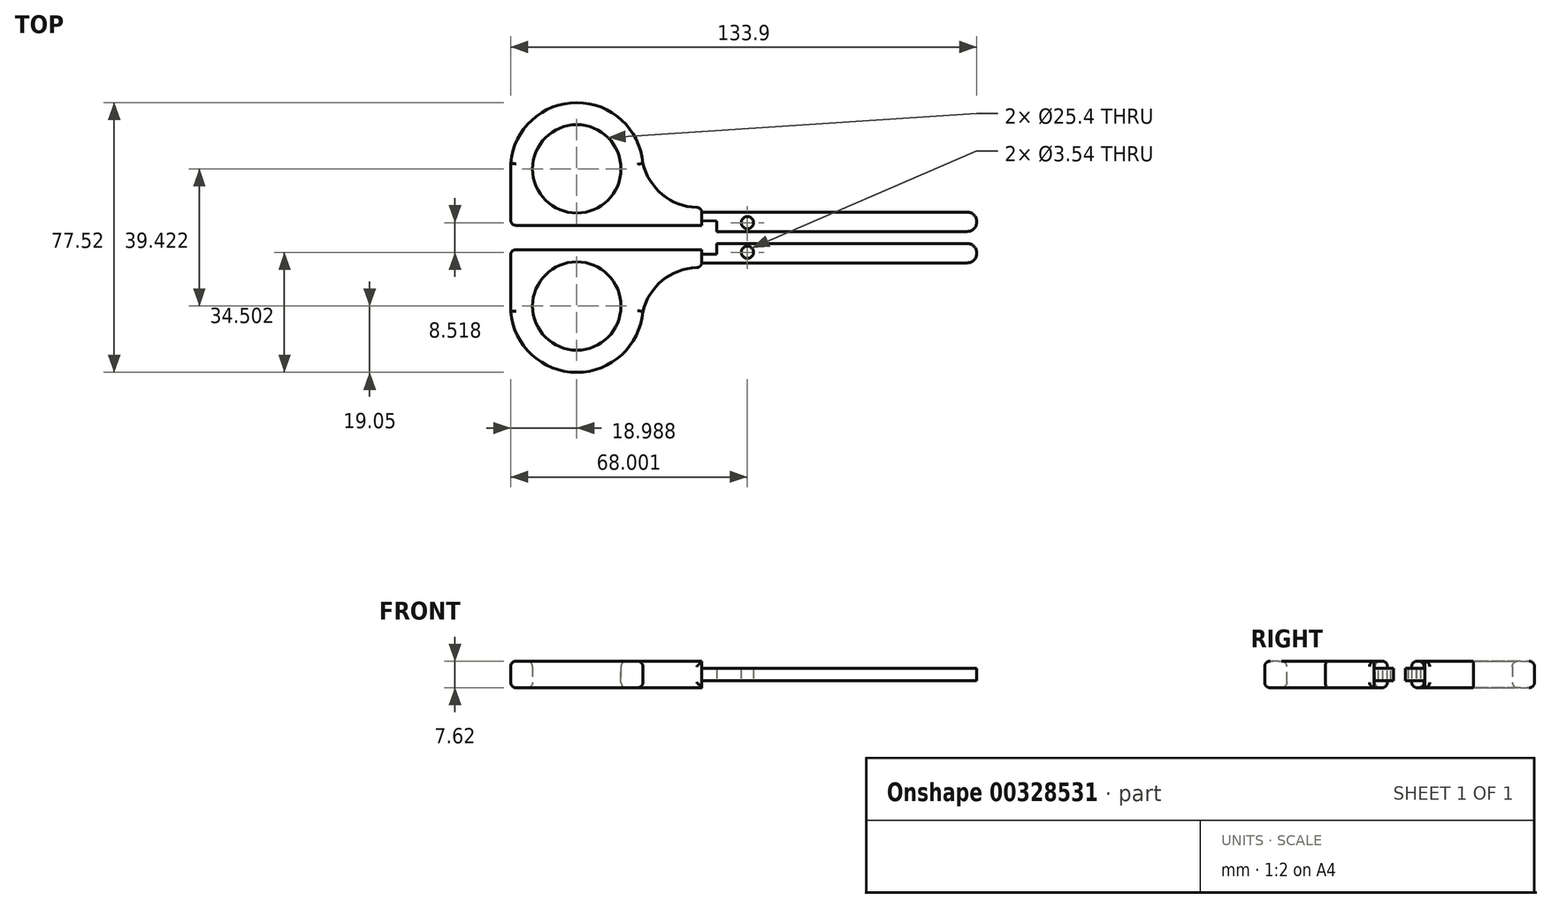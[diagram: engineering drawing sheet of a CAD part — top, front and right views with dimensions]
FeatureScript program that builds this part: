
annotation { "Feature Type Name" : "Feature", "Feature Type Description" : "" }
export const myFeature = defineFeature(function(context is Context, id is Id, definition is map)
    precondition{}
    {
        {
            var Q0;
            Q0=qCreatedBy(makeId("Top.planeOp"),FACE);
            var sketch = newSketch(context, id + "F0", { "sketchPlane" : qUnion([Q0])});
            skLineSegment(sketch, "E0", {"start": v(-55.55, 12.67) * mm, "end": v(-55.55, -5.11) * mm});
            skArc(sketch, "E1", {"start": v(-17.58, 12.67) * mm, "mid": v(-36.56, 30.16) * mm, "end": v(-55.55, 12.67) * mm});
            skLineSegment(sketch, "E2", {"start": v(-0.64, -1.3) * mm, "end": v(-0.64, -3.77) * mm});
            skLineSegment(sketch, "E3", {"start": v(-1.57, -5.11) * mm, "end": v(-55.55, -5.11) * mm});
            skCircle(sketch, "E4", {"center": v(-36.56, 11.11) * mm, "radius": 12.7 * mm});
            skLineSegment(sketch, "E5", {"start": v(-0.64, -1.3) * mm, "end": v(75.56, -1.3) * mm});
            skLineSegment(sketch, "E6", {"start": v(-0.64, -3.77) * mm, "end": v(3.68, -3.84) * mm});
            skCircle(sketch, "E7", {"center": v(12.45, -4.34) * mm, "radius": 1.77 * mm});
            skLineSegment(sketch, "E8", {"start": v(75.56, -6.88) * mm, "end": v(3.68, -6.88) * mm});
            skArc(sketch, "E9", {"start": v(75.56, -1.3) * mm, "mid": v(78.35, -4.09) * mm, "end": v(75.56, -6.88) * mm});
            skArc(sketch, "E10", {"start": v(-2.1, 0.05) * mm, "mid": v(-11.96, 3.75) * mm, "end": v(-17.58, 12.67) * mm});
            skArc(sketch, "E11", {"start": v(-2.1, 0.05) * mm, "mid": v(-1.12, -0.35) * mm, "end": v(-0.64, -1.3) * mm});
            skLineSegment(sketch, "E12", {"start": v(-1.57, -5.11) * mm, "end": v(-0.64, -5.11) * mm});
            skLineSegment(sketch, "E13", {"start": v(-0.64, -5.11) * mm, "end": v(-0.64, -3.77) * mm});
            skLineSegment(sketch, "E14", {"start": v(3.68, -3.84) * mm, "end": v(3.68, -6.88) * mm});
            skLineSegment(sketch, "E15", {"start": v(-93.56, -8.6) * mm, "end": v(102.9, -8.6) * mm});
            skSolve(sketch);
        }
        {
            var Q0;
            Q0=makeQuery(id+"F0.imprint","IMPRINT",FACE,{"disambiguationData":[TD([[makeQuery(id+"F0.imprint","IMPRINT",EDGE,{"derivedFrom":sQuery(id+"F0.wireOp",EDGE,"E0")}),1.0]])]});
            extrude(context, id + "F1", {"entities" : qUnion([Q0]), "endBound" : BoundingType.SYMMETRIC, "depth" : 7.62 * mm});
        }
        {
            var Q0;
            Q0=makeQuery(id+"F0.imprint","IMPRINT",FACE,{"disambiguationData":[TD([[makeQuery(id+"F0.imprint","IMPRINT",EDGE,{"derivedFrom":sQuery(id+"F0.wireOp",EDGE,"E2")}),1.0]])]});
            extrude(context, id + "F2", {"entities" : qUnion([Q0]), "operationType" : NewBodyOperationType.ADD, "endBound" : BoundingType.SYMMETRIC, "depth" : 3.63 * mm});
        }
        {
            var Q0;
            Q0=makeQuery(id+"F1.opExtrude","SWEPT_BODY",BODY,{"disambiguationData":[OSD([sQuery(id+"F0.wireOp",EDGE,"E0"),sQuery(id+"F0.wireOp",EDGE,"E1"),sQuery(id+"F0.wireOp",EDGE,"E2"),sQuery(id+"F0.wireOp",EDGE,"E3"),sQuery(id+"F0.wireOp",EDGE,"E4"),sQuery(id+"F0.wireOp",EDGE,"E10"),sQuery(id+"F0.wireOp",EDGE,"E11"),sQuery(id+"F0.wireOp",EDGE,"E12"),sQuery(id+"F0.wireOp",EDGE,"E13")])]});
            var Q1;
            Q1=sQuery(id+"F0.wireOp",EDGE,"E15");
            transform(context, id + "F3", {"entities" : qUnion([Q0]), "transformType" : TransformType.ROTATION, "transformAxis" : qUnion([Q1]), "angle" : 180 * degree, "makeCopy" : false});
        }
        {
            var Q0;
            Q0=makeQuery(id+"F0.imprint","IMPRINT",FACE,{"disambiguationData":[TD([[makeQuery(id+"F0.imprint","IMPRINT",EDGE,{"derivedFrom":sQuery(id+"F0.wireOp",EDGE,"E0")}),1.0]])]});
            extrude(context, id + "F4", {"entities" : qUnion([Q0]), "endBound" : BoundingType.SYMMETRIC, "depth" : 7.62 * mm});
        }
        {
            var Q0;
            Q0=makeQuery(id+"F0.imprint","IMPRINT",FACE,{"disambiguationData":[TD([[makeQuery(id+"F0.imprint","IMPRINT",EDGE,{"derivedFrom":sQuery(id+"F0.wireOp",EDGE,"E2")}),1.0]])]});
            extrude(context, id + "F5", {"entities" : qUnion([Q0]), "operationType" : NewBodyOperationType.ADD, "endBound" : BoundingType.SYMMETRIC, "depth" : 3.63 * mm});
        }
        {
            var Q0;
            Q0=makeQuery(id+"F1.opExtrude","CAP_EDGE",EDGE,{"disambiguationData":[OSD([sQuery(id+"F0.wireOp",EDGE,"E10")])],"isStart":true});
            var Q1;
            Q1=makeQuery(id+"F1.opExtrude","CAP_EDGE",EDGE,{"disambiguationData":[OSD([sQuery(id+"F0.wireOp",EDGE,"E10")])],"isStart":false});
            var Q2;
            Q2=makeQuery(id+"F4.opExtrude","CAP_EDGE",EDGE,{"disambiguationData":[OSD([sQuery(id+"F0.wireOp",EDGE,"E10")])],"isStart":false});
            var Q3;
            Q3=makeQuery(id+"F4.opExtrude","CAP_EDGE",EDGE,{"disambiguationData":[OSD([sQuery(id+"F0.wireOp",EDGE,"E10")])],"isStart":true});
            fillet(context, id + "F6", {"entities" : qUnion([Q0, Q1, Q2, Q3]), "radius" : 1.52 * mm, "tangentPropagation" : true, "allowEdgeOverflow" : false});
        }
        {
            var Q0;
            Q0=makeQuery(id+"F1.opExtrude","CAP_EDGE",EDGE,{"disambiguationData":[OSD([sQuery(id+"F0.wireOp",EDGE,"E1")])],"isStart":true});
            var Q1;
            Q1=makeQuery(id+"F1.opExtrude","CAP_EDGE",EDGE,{"disambiguationData":[OSD([sQuery(id+"F0.wireOp",EDGE,"E1")])],"isStart":false});
            var Q2;
            Q2=makeQuery(id+"F4.opExtrude","CAP_EDGE",EDGE,{"disambiguationData":[OSD([sQuery(id+"F0.wireOp",EDGE,"E1")])],"isStart":false});
            var Q3;
            Q3=makeQuery(id+"F4.opExtrude","CAP_EDGE",EDGE,{"disambiguationData":[OSD([sQuery(id+"F0.wireOp",EDGE,"E1")])],"isStart":true});
            fillet(context, id + "F7", {"entities" : qUnion([Q0, Q1, Q2, Q3]), "radius" : 1.52 * mm, "tangentPropagation" : true, "allowEdgeOverflow" : false});
        }
        {
            var Q0;
            Q0=makeQuery(id+"F1.opExtrude","CAP_EDGE",EDGE,{"disambiguationData":[OSD([sQuery(id+"F0.wireOp",EDGE,"E4")])],"isStart":true});
            var Q1;
            Q1=makeQuery(id+"F1.opExtrude","CAP_EDGE",EDGE,{"disambiguationData":[OSD([sQuery(id+"F0.wireOp",EDGE,"E4")])],"isStart":false});
            var Q2;
            Q2=makeQuery(id+"F4.opExtrude","CAP_EDGE",EDGE,{"disambiguationData":[OSD([sQuery(id+"F0.wireOp",EDGE,"E4")])],"isStart":false});
            var Q3;
            Q3=makeQuery(id+"F4.opExtrude","CAP_EDGE",EDGE,{"disambiguationData":[OSD([sQuery(id+"F0.wireOp",EDGE,"E4")])],"isStart":true});
            fillet(context, id + "F8", {"entities" : qUnion([Q0, Q1, Q2, Q3]), "radius" : 1.52 * mm, "tangentPropagation" : true, "allowEdgeOverflow" : false});
        }
        {
            var Q0;
            Q0=makeQuery(id+"F4.opExtrude","CAP_EDGE",EDGE,{"disambiguationData":[OSD([sQuery(id+"F0.wireOp",EDGE,"E3"),sQuery(id+"F0.wireOp",EDGE,"E12")])],"isStart":false});
            var Q1;
            Q1=makeQuery(id+"F4.opExtrude","CAP_EDGE",EDGE,{"disambiguationData":[OSD([sQuery(id+"F0.wireOp",EDGE,"E3"),sQuery(id+"F0.wireOp",EDGE,"E12")])],"isStart":true});
            var Q2;
            Q2=makeQuery(id+"F1.opExtrude","CAP_EDGE",EDGE,{"disambiguationData":[OSD([sQuery(id+"F0.wireOp",EDGE,"E3"),sQuery(id+"F0.wireOp",EDGE,"E12")])],"isStart":false});
            var Q3;
            Q3=makeQuery(id+"F1.opExtrude","CAP_EDGE",EDGE,{"disambiguationData":[OSD([sQuery(id+"F0.wireOp",EDGE,"E3"),sQuery(id+"F0.wireOp",EDGE,"E12")])],"isStart":true});
            fillet(context, id + "F9", {"entities" : qUnion([Q0, Q1, Q2, Q3]), "radius" : 1.52 * mm, "tangentPropagation" : true, "allowEdgeOverflow" : false});
        }
    });
